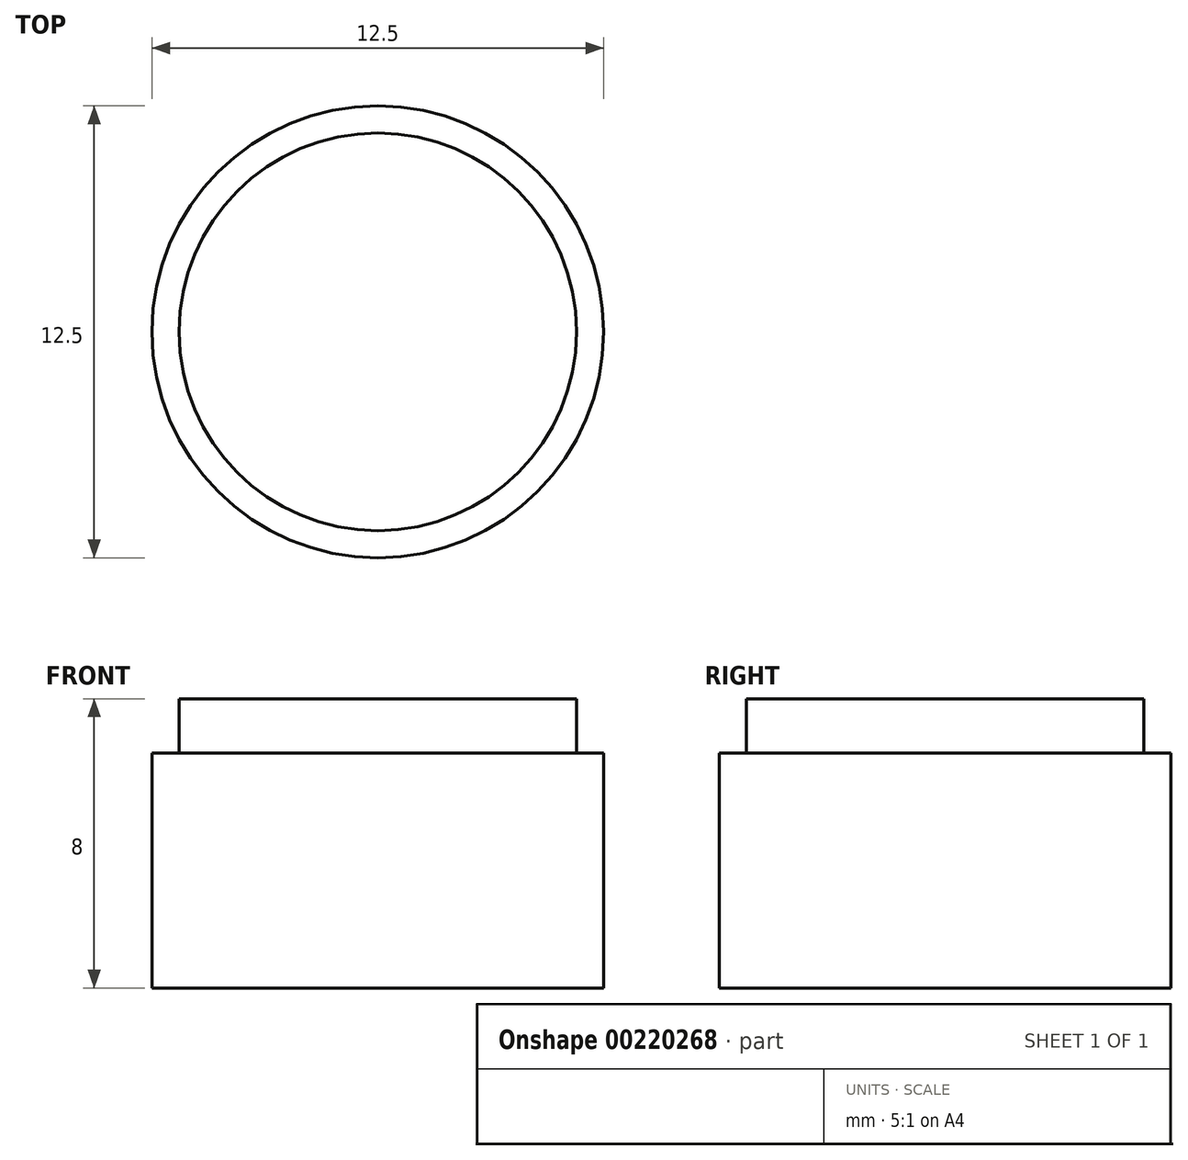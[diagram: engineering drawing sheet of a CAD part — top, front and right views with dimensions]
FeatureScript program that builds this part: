
annotation { "Feature Type Name" : "Feature", "Feature Type Description" : "" }
export const myFeature = defineFeature(function(context is Context, id is Id, definition is map)
    precondition{}
    {
        {
            var Q0;
            Q0=qCreatedBy(makeId("Top.planeOp"),FACE);
            var sketch = newSketch(context, id + "F0", { "sketchPlane" : qUnion([Q0])});
            skCircle(sketch, "E0", {"center": v(0, 0) * mm, "radius": 6.25 * mm});
            skSolve(sketch);
        }
        {
            var Q0;
            Q0 = qSketchRegion(id + "F0", true);
            var Q1;
            Q1=sQuery(id+"F0.wireOp",EDGE,"E0");
            extrude(context, id + "F1", {"entities" : qUnion([Q0]), "surfaceEntities" : qUnion([Q1]), "depth" : 8 * mm});
        }
        {
            var Q0;
            Q0=makeQuery(id+"F1.opExtrude","CAP_FACE",FACE,{"disambiguationData":[OSD([sQuery(id+"F0.wireOp",EDGE,"E0")])],"isStart":false});
            var sketch = newSketch(context, id + "F2", { "sketchPlane" : qUnion([Q0])});
            skCircle(sketch, "E1", {"center": v(0, 0) * mm, "radius": 5.5 * mm});
            skSolve(sketch);
        }
        {
            var Q0;
            Q0=makeQuery(id+"F2.imprint","IMPRINT",FACE,{"disambiguationData":[TD([[makeQuery(id+"F2.imprint","IMPRINT",EDGE,{"derivedFrom":sQuery(id+"F2.wireOp",EDGE,"E1")}),-1.0]])]});
            var Q1;
            Q1=sQuery(id+"F2.wireOp",EDGE,"E1");
            extrude(context, id + "F3", {"entities" : qUnion([Q0]), "operationType" : NewBodyOperationType.REMOVE, "surfaceEntities" : qUnion([Q1]), "oppositeDirection" : true, "depth" : 1.5 * mm});
        }
    });
